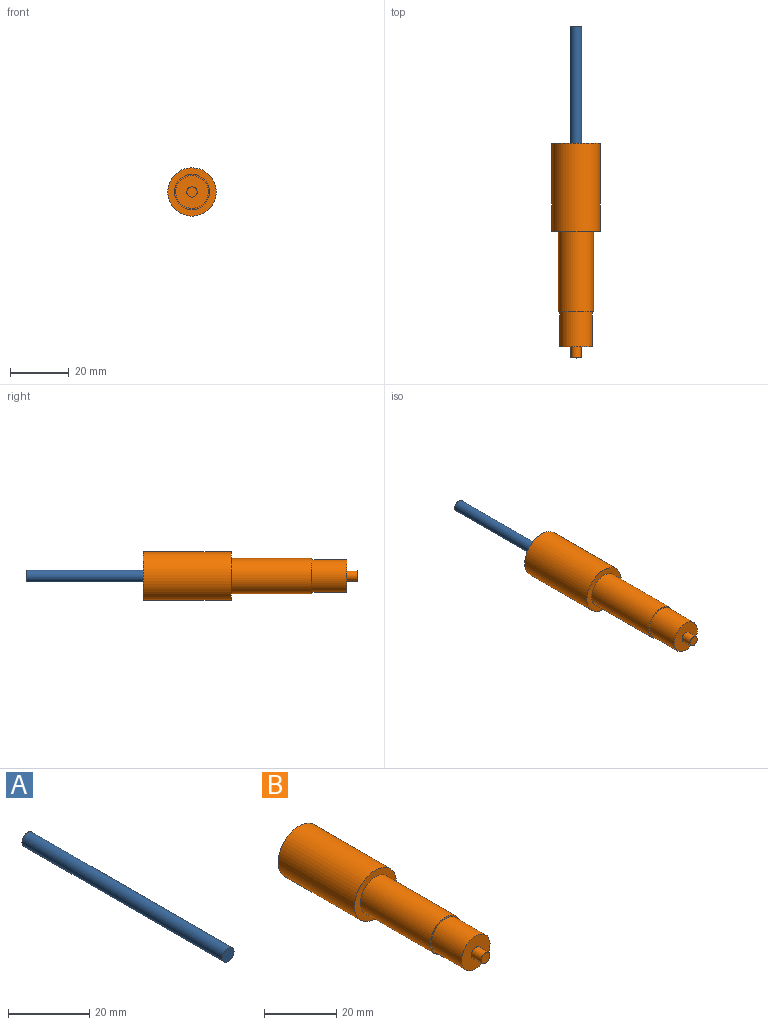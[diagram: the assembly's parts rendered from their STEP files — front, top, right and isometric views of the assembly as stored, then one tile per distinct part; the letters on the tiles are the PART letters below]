
ASSEMBLY  parts=2 mates=1
PART A: 3 faces, bbox 4x70x4 mm
  f0: cylinder r=2mm len=70mm, axis (0,1,0), area 879.6mm2, adj f1,f2
  f1: plane 4x4mm, normal (0,-1,0), area 12.6mm2, adj f0
  f2: plane 4x4mm, normal (0,1,0), area 12.6mm2, adj f0
PART B: 11 faces, bbox 16.5x73.2x16.5 mm
  f0: cylinder r=8.25mm len=30mm, axis (0,1,0), area 1555.1mm2, adj f1,f2
  f1: plane 16.5x16.5mm, normal (0,-1,0), area 101.1mm2, adj f0,f3
  f2: plane 16.5x16.5mm, normal (0,1,0), area 201.3mm2, adj f0,f9
  f3: cylinder r=5.99mm len=27.5mm, axis (0,1,0), area 1035mm2, adj f1,f4
  f4: plane 11.98x11.98mm, normal (0,-1,0), area 14.9mm2, adj f3,f5
  f5: cylinder r=5.58mm len=11.9mm, axis (0,1,0), area 417.2mm2, adj f4,f6
  f6: plane 11.16x11.16mm, normal (0,-1,0), area 88.2mm2, adj f5,f7
  f7: cylinder r=1.75mm len=3.8mm, axis (0,1,0), area 41.8mm2, adj f6,f8
  f8: plane 3.5x3.5mm, normal (0,-1,0), area 9.6mm2, adj f7
  f9: cylinder r=2mm len=25mm, axis (0,1,0), area 314.2mm2, adj f2,f10
  f10: plane 4x4mm, normal (0,1,0), area 12.6mm2, adj f9
PLACE A t=(-32.45,1.33,-13.4)mm
PLACE B t=(-32.45,-38.67,-13.4)mm
MATE fastened B.f0 <-> A.f0  axis (0,1,0) through (-32.45,-68.67,-13.4)mm
